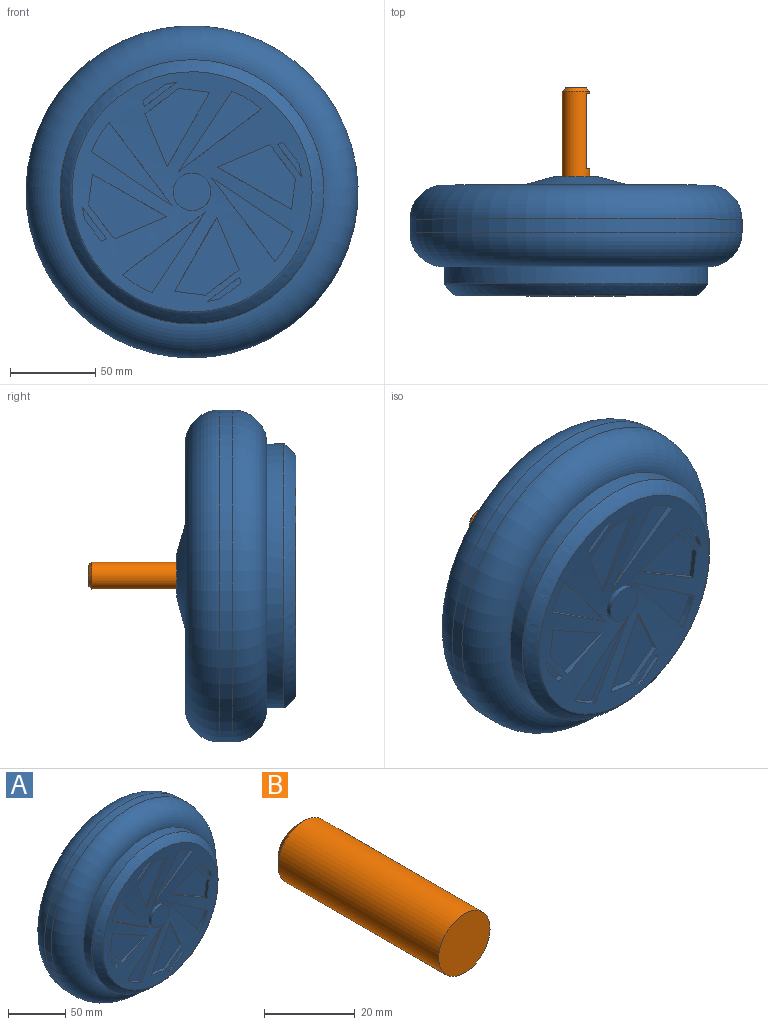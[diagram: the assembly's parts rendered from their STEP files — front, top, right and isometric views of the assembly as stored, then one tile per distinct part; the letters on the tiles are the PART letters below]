
ASSEMBLY  parts=2 mates=1
PART A: 82 faces, bbox 214.4x73.2x214.4 mm
  f0: cone r=0mm half-angle=59deg, axis (0,1,0), area 18.6mm2, adj f1
  f1: cylinder r=2.25mm len=14.4mm, axis (0,1,0), area 203.6mm2, adj f0,f15
  f2: cone r=0mm half-angle=59deg, axis (0,1,0), area 18.6mm2, adj f3
  f3: cylinder r=2.25mm len=14.4mm, axis (0,1,0), area 203.6mm2, adj f2,f15
  f4: cone r=0mm half-angle=59deg, axis (0,1,0), area 18.6mm2, adj f5
  f5: cylinder r=2.25mm len=14.4mm, axis (0,1,0), area 203.6mm2, adj f4,f15
  f6: cone r=0mm half-angle=59deg, axis (0,1,0), area 18.6mm2, adj f7
  f7: cylinder r=2.25mm len=14.4mm, axis (0,1,0), area 203.6mm2, adj f6,f15
  f8: cone r=0mm half-angle=59deg, axis (0,1,0), area 18.6mm2, adj f9
  f9: cylinder r=2.25mm len=14.4mm, axis (0,1,0), area 203.6mm2, adj f8,f15
  f10: cylinder r=97.5mm len=195mm, axis (0,1,0), area 4900.9mm2, adj f12,f13
  f11: plane 155x155mm, normal (0,1,0), area 3694.5mm2, adj f12,f14
  f12: torus R=77.5mm, axis (0,-1,0), area 17811.2mm2, adj f10,f11
  f13: torus R=77.5mm, axis (0,-1,0), area 17811.2mm2, adj f10,f21
  f14: torus R=69.5mm, axis (0,-1,0), area 679.7mm2, adj f11,f16
  f15: plane 137x137mm, normal (0,1,0), area 11593mm2, adj f1,f3,f5,f7,f9,f16,f18,f20
  f16: cylinder r=68.5mm len=137mm, axis (0,1,0), area 430.4mm2, adj f14,f15
  f17: plane 25.85x25.85mm, normal (0,1,0), area 524.6mm2, adj f18
  f18: cone r=31.58mm half-angle=75deg, axis (0,-1,0), area 2617.3mm2, adj f15,f17
  f19: cone r=0mm half-angle=59deg, axis (0,1,0), area 18.6mm2, adj f20
  f20: cylinder r=2.25mm len=14.4mm, axis (0,1,0), area 203.6mm2, adj f15,f19
  f21: cylinder r=77.5mm len=155mm, axis (0,1,0), area 4869.5mm2, adj f13,f22
  f22: bspline ~154.92x154.84mm, area 4682.8mm2, adj f21,f23
  f23: cone r=11.05mm half-angle=87.1deg, axis (0,-1,0), area 9246mm2, adj f22,f24,f26,f27,f28,f30,f31,f32
  f24: cylinder r=11.05mm len=22.1mm, axis (0,1,0), area 208.3mm2, adj f23,f76
  f25: plane 48.85x47.38mm, normal (0,-1,0), area 587.1mm2, adj f26,f27,f28
  f26: cylinder r=63.58mm len=17.43mm, axis (0,-1,0), area 74.4mm2, adj f23,f25,f27,f28
  f27: plane 50.62x38.75mm, normal (0.6,0,-0.8), area 137.1mm2, adj f23,f25,f26,f28
  f28: plane 50.67x34.72mm, normal (-0.83,0,0.55), area 131.1mm2, adj f23,f25,f26,f27
  f29: plane 19.88x14.14mm, normal (0,-1,0), area 64.3mm2, adj f30,f31,f32,f33
  f30: cylinder r=64.97mm len=7.14mm, axis (0,-1,0), area 27.1mm2, adj f23,f29,f31,f33
  f31: plane 20.98x16.58mm, normal (0.61,0,-0.8), area 81.5mm2, adj f23,f29,f30,f32
  f32: plane 3.52x3.17mm, normal (-0.92,0,-0.39), area 11.7mm2, adj f23,f29,f31,f33
  f33: plane 13.82x10.63mm, normal (-0.6,0,0.8), area 57.3mm2, adj f23,f29,f30,f32
  f34: plane 45.97x38mm, normal (0,-1,0), area 830.2mm2, adj f35,f36,f37,f38
  f35: plane 30.96x13.13mm, normal (-0.92,0,-0.39), area 77.6mm2, adj f23,f34,f36,f38
  f36: plane 22.91x17.98mm, normal (-0.6,0,0.8), area 82.2mm2, adj f23,f34,f35,f37
  f37: plane 18.52x3.99mm, normal (0.13,0,0.99), area 63mm2, adj f23,f34,f36,f38
  f38: plane 45.33x26.57mm, normal (0.87,0,-0.5), area 117.6mm2, adj f23,f34,f35,f37
  f39: plane 48.85x47.38mm, normal (0,-1,0), area 587.1mm2, adj f40,f41,f42
  f40: cylinder r=63.58mm len=17.43mm, axis (0,-1,0), area 74.4mm2, adj f23,f39,f41,f42
  f41: plane 48.86x36.98mm, normal (-0.6,0,0.8), area 137.1mm2, adj f23,f39,f40,f42
  f42: plane 47.38x31.43mm, normal (0.83,0,-0.55), area 131.1mm2, adj f23,f39,f40,f41
  f43: plane 19.88x14.14mm, normal (0,-1,0), area 64.3mm2, adj f44,f45,f46,f47
  f44: cylinder r=64.97mm len=7.14mm, axis (0,-1,0), area 27.1mm2, adj f23,f43,f45,f47
  f45: plane 20.98x16.58mm, normal (-0.61,0,0.8), area 81.5mm2, adj f23,f43,f44,f46
  f46: plane 3.52x3.17mm, normal (0.92,0,0.39), area 11.7mm2, adj f23,f43,f45,f47
  f47: plane 13.82x10.63mm, normal (0.6,0,-0.8), area 57.3mm2, adj f23,f43,f44,f46
  f48: plane 45.97x38mm, normal (0,-1,0), area 830.2mm2, adj f49,f50,f51,f52
  f49: plane 30.96x13.13mm, normal (0.39,0,-0.92), area 77.6mm2, adj f23,f48,f50,f52
  f50: plane 22.91x17.98mm, normal (-0.8,0,-0.6), area 82.2mm2, adj f23,f48,f49,f51
  f51: plane 19.46x4.93mm, normal (-0.99,0,0.13), area 63mm2, adj f23,f48,f50,f52
  f52: plane 43.63x24.86mm, normal (0.5,0,0.87), area 117.6mm2, adj f23,f48,f49,f51
  f53: plane 48.85x47.38mm, normal (0,-1,0), area 587.1mm2, adj f54,f55,f56
  f54: cylinder r=63.58mm len=17.43mm, axis (0,-1,0), area 74.4mm2, adj f23,f53,f55,f56
  f55: plane 48.86x36.98mm, normal (0.8,0,0.6), area 137.1mm2, adj f23,f53,f54,f56
  f56: plane 47.38x31.43mm, normal (-0.55,0,-0.83), area 131.1mm2, adj f23,f53,f54,f55
  f57: plane 19.88x14.14mm, normal (0,-1,0), area 64.3mm2, adj f58,f59,f60,f61
  f58: cylinder r=64.97mm len=7.14mm, axis (0,-1,0), area 27.1mm2, adj f23,f57,f59,f61
  f59: plane 20.98x16.58mm, normal (-0.8,0,-0.61), area 81.5mm2, adj f23,f57,f58,f60
  f60: plane 3.52x3.17mm, normal (-0.39,0,0.92), area 11.7mm2, adj f23,f57,f59,f61
  f61: plane 13.82x10.63mm, normal (0.8,0,0.6), area 57.3mm2, adj f23,f57,f58,f60
  f62: plane 48.85x47.38mm, normal (0,-1,0), area 587.1mm2, adj f63,f64,f65
  f63: cylinder r=63.58mm len=17.43mm, axis (0,-1,0), area 74.4mm2, adj f23,f62,f64,f65
  f64: plane 48.86x36.98mm, normal (-0.8,0,-0.6), area 137.1mm2, adj f23,f62,f63,f65
  f65: plane 47.38x31.43mm, normal (0.55,0,0.83), area 131.1mm2, adj f23,f62,f63,f64
  f66: plane 45.97x38mm, normal (0,-1,0), area 830.2mm2, adj f67,f68,f69,f70
  f67: plane 30.96x13.13mm, normal (-0.39,0,0.92), area 77.6mm2, adj f23,f66,f68,f70
  f68: plane 22.91x17.98mm, normal (0.8,0,0.6), area 82.2mm2, adj f23,f66,f67,f69
  f69: plane 19.46x4.93mm, normal (0.99,0,-0.13), area 63mm2, adj f23,f66,f68,f70
  f70: plane 43.63x24.86mm, normal (-0.5,0,-0.87), area 117.6mm2, adj f23,f66,f67,f69
  f71: plane 45.97x38mm, normal (0,-1,0), area 830.2mm2, adj f72,f73,f74,f75
  f72: plane 30.96x13.13mm, normal (0.92,0,0.39), area 77.6mm2, adj f23,f71,f73,f75
  f73: plane 22.91x17.98mm, normal (0.6,0,-0.8), area 82.2mm2, adj f23,f71,f72,f74
  f74: plane 19.46x4.93mm, normal (-0.13,0,-0.99), area 63mm2, adj f23,f71,f73,f75
  f75: plane 43.63x24.86mm, normal (-0.87,0,0.5), area 117.6mm2, adj f23,f71,f72,f74
  f76: plane 22.1x22.1mm, normal (0,-1,0), area 383.6mm2, adj f24
  f77: plane 19.88x14.14mm, normal (0,-1,0), area 64.3mm2, adj f78,f79,f80,f81
  f78: cylinder r=64.97mm len=7.14mm, axis (0,-1,0), area 27.1mm2, adj f23,f77,f79,f81
  f79: plane 20.98x16.58mm, normal (0.8,0,0.61), area 81.5mm2, adj f23,f77,f78,f80
  f80: plane 3.52x3.17mm, normal (0.39,0,-0.92), area 11.7mm2, adj f23,f77,f79,f81
  f81: plane 13.82x10.63mm, normal (-0.8,0,-0.6), area 57.3mm2, adj f23,f77,f78,f80
PART B: 9 faces, bbox 16x52.1x16 mm
  f0: cylinder r=8mm len=50.11mm, axis (0,-1,0), area 1914.8mm2, adj f2,f5,f6,f7,f8
  f1: plane 12x12mm, normal (0,1,0), area 62.8mm2, adj f3,f8
  f2: plane 16x16mm, normal (0,-1,0), area 201.1mm2, adj f0
  f3: cylinder r=4mm len=47.46mm, axis (0,-1,0), area 1192.8mm2, adj f1,f4
  f4: plane 8x8mm, normal (0,1,0), area 50.3mm2, adj f3
  f5: plane 44.5x11.82mm, normal (0.99,0,-0.17), area 534.1mm2, adj f0,f6,f7
  f6: plane 11.82x3.82mm, normal (0,-1,0), area 22.5mm2, adj f0,f5
  f7: plane 11.82x3.82mm, normal (0,1,0), area 22.5mm2, adj f0,f5
  f8: cone r=6mm half-angle=45deg, axis (0,-1,0), area 124.4mm2, adj f0,f1
PLACE A t=(80.23,27.12,-124.77)mm
PLACE B t=(80.23,27.12,-124.77)mm
MATE revolute A.f18 <-> B.f0  axis (0,1,0) through (80.23,32.01,-124.77)mm
